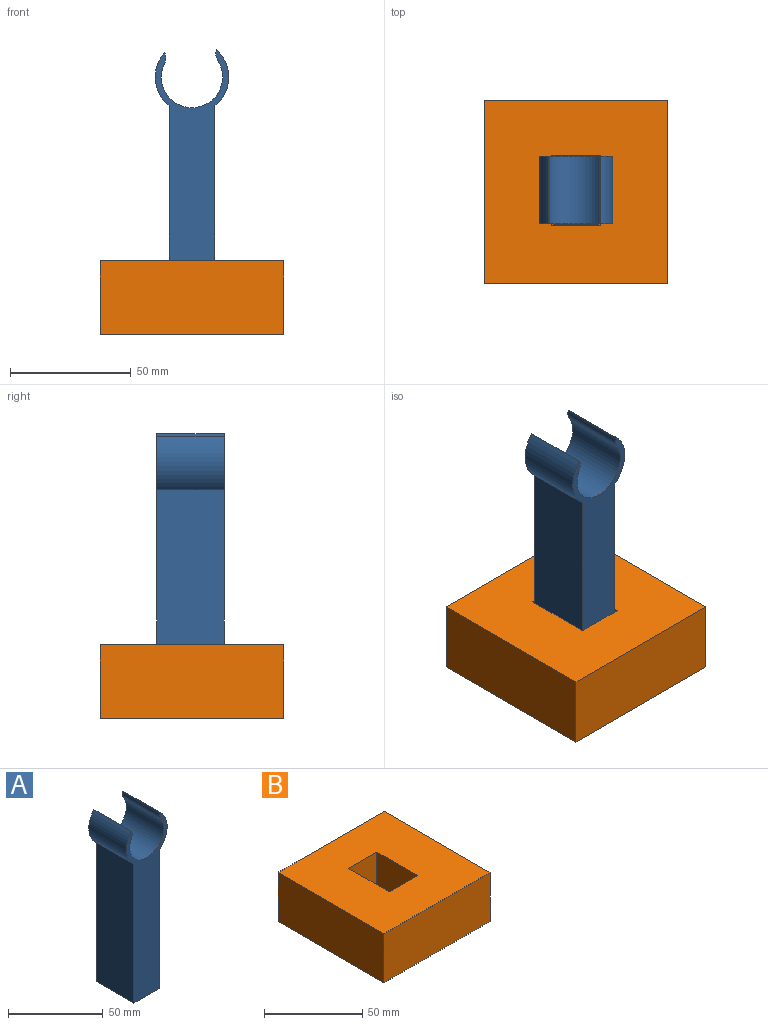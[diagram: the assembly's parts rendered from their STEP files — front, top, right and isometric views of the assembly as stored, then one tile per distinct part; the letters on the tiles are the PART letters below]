
ASSEMBLY  parts=2 mates=1
PART A: 10 faces, bbox 30.5x27.9x113 mm
  f0: cylinder r=15.24mm len=27.94mm, axis (0,1,0), area 691.1mm2, adj f1,f5,f6,f7
  f1: plane 89.7x27.94mm, normal (-1,0,0), area 2506.3mm2, adj f0,f5,f6,f9
  f2: plane 89.7x27.94mm, normal (1,0,0), area 2506.3mm2, adj f3,f5,f6,f9
  f3: cylinder r=15.24mm len=27.94mm, axis (0,1,0), area 740.6mm2, adj f2,f5,f6,f8
  f4: cylinder r=12.7mm len=27.94mm, axis (0,1,0), area 1481.9mm2, adj f5,f6,f7,f8
  f5: plane 112.98x30.48mm, normal (0,-1,0), area 1827.7mm2, adj f0,f1,f2,f3,f4,f7,f8,f9
  f6: plane 112.98x30.48mm, normal (0,1,0), area 1827.7mm2, adj f0,f1,f2,f3,f4,f7,f8,f9
  f7: cylinder r=5.08mm len=27.94mm, axis (0,1,0), area 130.3mm2, adj f0,f4,f5,f6
  f8: cylinder r=5.08mm len=27.94mm, axis (0,1,0), area 130.3mm2, adj f3,f4,f5,f6
  f9: plane 27.94x19.05mm, normal (0,0,-1), area 532.3mm2, adj f1,f2,f5,f6
PART B: 11 faces, bbox 76.2x76.2x30.5 mm
  f0: plane 25.4x20.32mm, normal (0,-1,0), area 516.1mm2, adj f1,f7,f8,f9
  f1: plane 29.21x25.4mm, normal (1,0,0), area 741.9mm2, adj f0,f2,f8,f9
  f2: plane 25.4x20.32mm, normal (0,1,0), area 516.1mm2, adj f1,f7,f8,f9
  f3: plane 76.2x30.48mm, normal (-1,0,0), area 2322.6mm2, adj f4,f6,f8,f10
  f4: plane 76.2x30.48mm, normal (0,1,0), area 2322.6mm2, adj f3,f5,f8,f10
  f5: plane 76.2x30.48mm, normal (1,0,0), area 2322.6mm2, adj f4,f6,f8,f10
  f6: plane 76.2x30.48mm, normal (0,-1,0), area 2322.6mm2, adj f3,f5,f8,f10
  f7: plane 29.21x25.4mm, normal (-1,0,0), area 741.9mm2, adj f0,f2,f8,f9
  f8: plane 76.2x76.2mm, normal (0,0,1), area 5212.9mm2, adj f0,f1,f2,f3,f4,f5,f6,f7
  f9: plane 29.21x20.32mm, normal (0,0,1), area 593.5mm2, adj f0,f1,f2,f7
  f10: plane 76.2x76.2mm, normal (0,0,-1), area 5806.4mm2, adj f3,f4,f5,f6
PLACE A t=(-8.73,0.06,-31.31)mm
PLACE B t=(-8.88,0,-0.83)mm
MATE fastened A.f9 <-> B.f9  axis (0,0,-1) through (-8.73,-13.91,-132.91)mm
